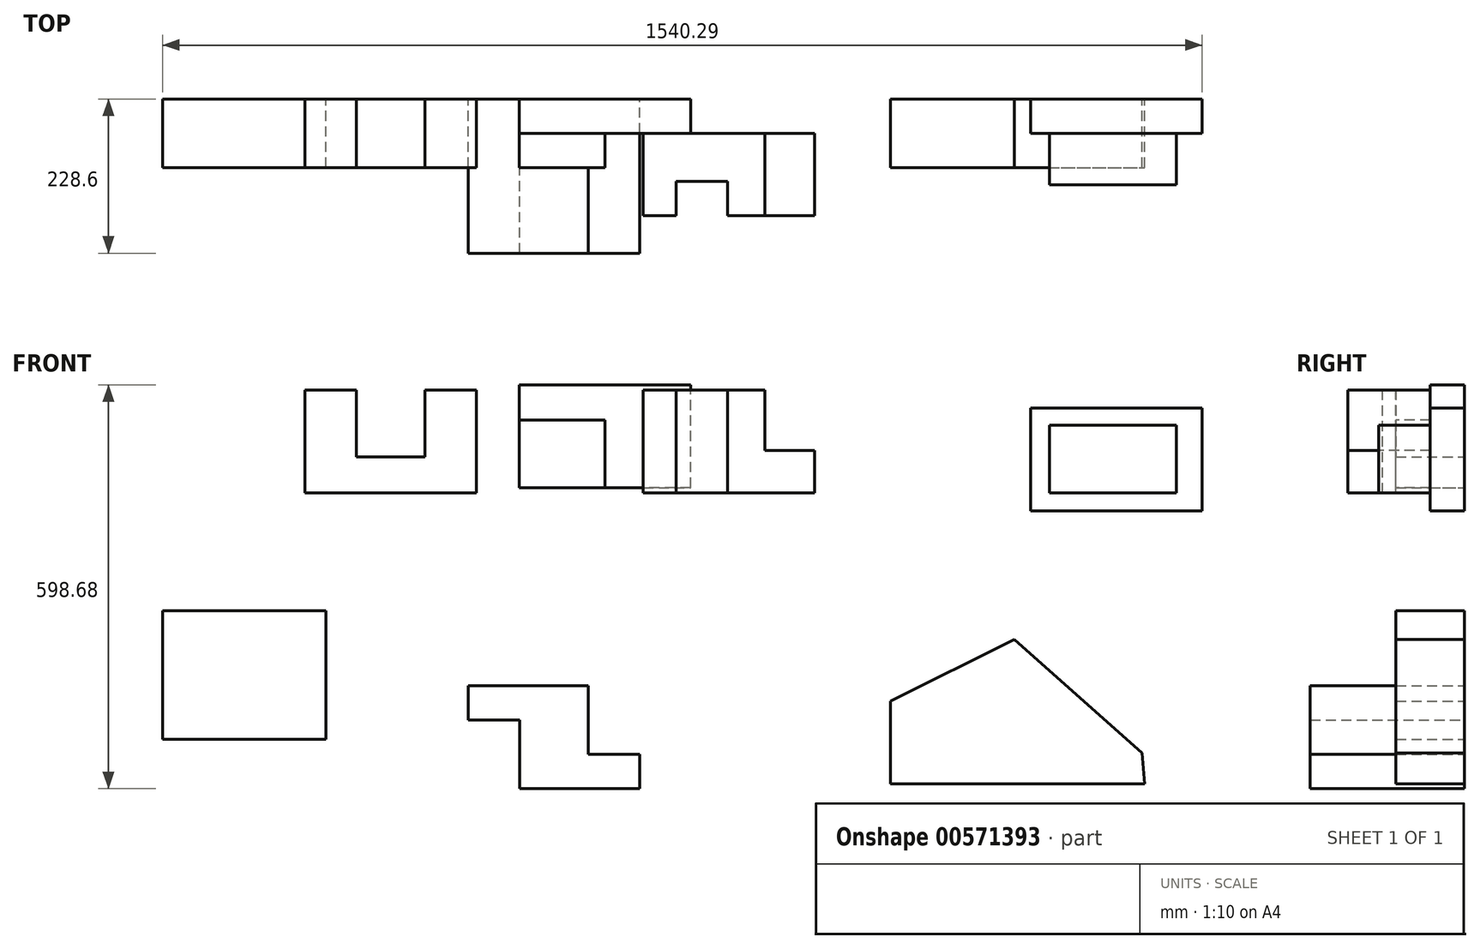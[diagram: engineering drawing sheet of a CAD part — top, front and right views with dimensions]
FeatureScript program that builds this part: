
annotation { "Feature Type Name" : "Feature", "Feature Type Description" : "" }
export const myFeature = defineFeature(function(context is Context, id is Id, definition is map)
    precondition{}
    {
        {
            var Q0;
            Q0=qCreatedBy(makeId("Front.planeOp"),FACE);
            var sketch = newSketch(context, id + "F0", { "sketchPlane" : qUnion([Q0])});
            skLineSegment(sketch, "E0", {"start": v(254, 0) * mm, "end": v(254, 152.4) * mm});
            skLineSegment(sketch, "E1", {"start": v(254, 152.4) * mm, "end": v(177.8, 152.4) * mm});
            skLineSegment(sketch, "E2", {"start": v(177.8, 152.4) * mm, "end": v(177.8, 53.07) * mm});
            skLineSegment(sketch, "E3", {"start": v(177.8, 53.07) * mm, "end": v(76.2, 53.07) * mm});
            skLineSegment(sketch, "E4", {"start": v(76.2, 53.07) * mm, "end": v(76.2, 152.4) * mm});
            skLineSegment(sketch, "E5", {"start": v(76.2, 152.4) * mm, "end": v(0, 152.4) * mm});
            skLineSegment(sketch, "E6", {"start": v(0, 152.4) * mm, "end": v(0, 0) * mm});
            skLineSegment(sketch, "E7", {"start": v(0, 0) * mm, "end": v(254, 0) * mm});
            skSolve(sketch);
        }
        {
            var Q0;
            Q0=makeQuery(id+"F0.imprint","IMPRINT",FACE,{"disambiguationData":[TD([[makeQuery(id+"F0.imprint","IMPRINT",EDGE,{"derivedFrom":sQuery(id+"F0.wireOp",EDGE,"E0")}),1.0]])]});
            extrude(context, id + "F1", {"entities" : qUnion([Q0]), "depth" : 101.6 * mm, "offsetDistance" : 25.4 * mm});
        }
        {
            var Q0;
            Q0=qCreatedBy(makeId("Front.planeOp"),FACE);
            var sketch = newSketch(context, id + "F2", { "sketchPlane" : qUnion([Q0])});
            skLineSegment(sketch, "E8.bottom", {"start": v(317.16, 7.63) * mm, "end": v(571.16, 7.63) * mm});
            skLineSegment(sketch, "E8.top", {"start": v(317.16, 160.03) * mm, "end": v(571.16, 160.03) * mm});
            skLineSegment(sketch, "E8.left", {"start": v(317.16, 7.63) * mm, "end": v(317.16, 160.03) * mm});
            skLineSegment(sketch, "E8.right", {"start": v(571.16, 7.63) * mm, "end": v(571.16, 160.03) * mm});
            skSolve(sketch);
        }
        {
            var Q0;
            Q0=makeQuery(id+"F2.imprint","IMPRINT",FACE,{"disambiguationData":[TD([[makeQuery(id+"F2.imprint","IMPRINT",EDGE,{"derivedFrom":sQuery(id+"F2.wireOp",EDGE,"E8.bottom")}),1.0]])]});
            extrude(context, id + "F3", {"entities" : qUnion([Q0]), "depth" : 101.6 * mm, "offsetDistance" : 25.4 * mm});
        }
        {
            var Q0;
            Q0=makeQuery(id+"F3.opExtrude","SWEPT_FACE",FACE,{"disambiguationData":[OSD([sQuery(id+"F2.wireOp",EDGE,"E8.top")])]});
            var sketch = newSketch(context, id + "F4", { "sketchPlane" : qUnion([Q0])});
            skLineSegment(sketch, "E9.bottom", {"start": v(571.16, -50.8) * mm, "end": v(444.16, -50.8) * mm});
            skLineSegment(sketch, "E9.top", {"start": v(571.16, -101.6) * mm, "end": v(444.16, -101.6) * mm});
            skLineSegment(sketch, "E9.left", {"start": v(571.16, -50.8) * mm, "end": v(571.16, -101.6) * mm});
            skLineSegment(sketch, "E9.right", {"start": v(444.16, -50.8) * mm, "end": v(444.16, -101.6) * mm});
            skSolve(sketch);
        }
        {
            var Q0;
            Q0=makeQuery(id+"F4.imprint","IMPRINT",FACE,{"disambiguationData":[TD([[makeQuery(id+"F4.imprint","IMPRINT",EDGE,{"derivedFrom":sQuery(id+"F4.wireOp",EDGE,"E9.bottom")}),1.0]])]});
            extrude(context, id + "F5", {"entities" : qUnion([Q0]), "operationType" : NewBodyOperationType.REMOVE, "oppositeDirection" : true, "depth" : 152.4 * mm, "offsetDistance" : 25.4 * mm});
        }
        {
            var Q0;
            Q0=makeQuery(id+"F3.opExtrude","CAP_FACE",FACE,{"disambiguationData":[OSD([sQuery(id+"F2.wireOp",EDGE,"E8.bottom"),sQuery(id+"F2.wireOp",EDGE,"E8.top"),sQuery(id+"F2.wireOp",EDGE,"E8.left"),sQuery(id+"F2.wireOp",EDGE,"E8.right")])],"isStart":false});
            var sketch = newSketch(context, id + "F6", { "sketchPlane" : qUnion([Q0])});
            skLineSegment(sketch, "E10.bottom", {"start": v(317.16, 160.03) * mm, "end": v(444.16, 160.03) * mm});
            skLineSegment(sketch, "E10.top", {"start": v(317.16, 107.58) * mm, "end": v(444.16, 107.58) * mm});
            skLineSegment(sketch, "E10.left", {"start": v(317.16, 160.03) * mm, "end": v(317.16, 107.58) * mm});
            skLineSegment(sketch, "E10.right", {"start": v(444.16, 160.03) * mm, "end": v(444.16, 107.58) * mm});
            skSolve(sketch);
        }
        {
            var Q0;
            Q0=makeQuery(id+"F6.imprint","IMPRINT",FACE,{"disambiguationData":[TD([[makeQuery(id+"F6.imprint","IMPRINT",EDGE,{"derivedFrom":sQuery(id+"F6.wireOp",EDGE,"E10.bottom")}),-1.0]])]});
            extrude(context, id + "F7", {"entities" : qUnion([Q0]), "operationType" : NewBodyOperationType.REMOVE, "oppositeDirection" : true, "depth" : 50.8 * mm, "offsetDistance" : 25.4 * mm});
        }
        {
            var Q0;
            Q0=makeQuery(id+"F7.boolean.opBoolean","MERGE",FACE,{"derivedFrom":[makeQuery(id+"F5.boolean.opBoolean","COPY",FACE,{"derivedFrom":makeQuery(id+"F5.opExtrude","SWEPT_FACE",FACE,{"disambiguationData":[OSD([sQuery(id+"F4.wireOp",EDGE,"E9.bottom")])]})}),makeQuery(id+"F7.opExtrude","CAP_FACE",FACE,{"disambiguationData":[OSD([sQuery(id+"F6.wireOp",EDGE,"E10.bottom"),sQuery(id+"F6.wireOp",EDGE,"E10.top"),sQuery(id+"F6.wireOp",EDGE,"E10.left"),sQuery(id+"F6.wireOp",EDGE,"E10.right")])],"isStart":false})]});
            var sketch = newSketch(context, id + "F8", { "sketchPlane" : qUnion([Q0])});
            skLineSegment(sketch, "E11.bottom", {"start": v(500.85, 152.4) * mm, "end": v(754.85, 152.4) * mm});
            skLineSegment(sketch, "E11.top", {"start": v(500.85, 0) * mm, "end": v(754.85, 0) * mm});
            skLineSegment(sketch, "E11.left", {"start": v(500.85, 152.4) * mm, "end": v(500.85, 0) * mm});
            skLineSegment(sketch, "E11.right", {"start": v(754.85, 152.4) * mm, "end": v(754.85, 0) * mm});
            skSolve(sketch);
        }
        {
            var Q0;
            Q0 = qSketchRegion(id + "F8", true);
            extrude(context, id + "F9", {"entities" : qUnion([Q0]), "operationType" : NewBodyOperationType.ADD, "depth" : 121.92 * mm, "offsetDistance" : 25.4 * mm});
        }
        {
            var Q0;
            Q0=makeQuery(id+"F9.opExtrude","CAP_FACE",FACE,{"disambiguationData":[OSD([sQuery(id+"F8.wireOp",EDGE,"E11.bottom"),sQuery(id+"F8.wireOp",EDGE,"E11.top"),sQuery(id+"F8.wireOp",EDGE,"E11.left"),sQuery(id+"F8.wireOp",EDGE,"E11.right")])],"isStart":false});
            var sketch = newSketch(context, id + "F10", { "sketchPlane" : qUnion([Q0])});
            skLineSegment(sketch, "E12.bottom", {"start": v(551.65, 152.4) * mm, "end": v(500.85, 152.4) * mm});
            skLineSegment(sketch, "E12.top", {"start": v(551.65, 0) * mm, "end": v(500.85, 0) * mm});
            skLineSegment(sketch, "E12.left", {"start": v(551.65, 152.4) * mm, "end": v(551.65, 0) * mm});
            skLineSegment(sketch, "E12.right", {"start": v(500.85, 152.4) * mm, "end": v(500.85, 0) * mm});
            skSolve(sketch);
        }
        {
            var Q0;
            {var subQ0=sQuery(id+"F10.wireOp",EDGE,"E12.left");Q0=makeQuery(id+"F10.imprint","IMPRINT",FACE,{"disambiguationData":[TD([[makeQuery(id+"F10.imprint","IMPRINT",EDGE,{"derivedFrom":subQ0}),1.0]])]});}
            var sketch = newSketch(context, id + "F11", { "sketchPlane" : qUnion([Q0])});
            skLineSegment(sketch, "E13.bottom", {"start": v(757.59, 164.43) * mm, "end": v(681.39, 164.43) * mm});
            skLineSegment(sketch, "E13.top", {"start": v(757.59, 62.83) * mm, "end": v(681.39, 62.83) * mm});
            skLineSegment(sketch, "E13.left", {"start": v(757.59, 164.43) * mm, "end": v(757.59, 62.83) * mm});
            skLineSegment(sketch, "E13.right", {"start": v(681.39, 164.43) * mm, "end": v(681.39, 62.83) * mm});
            skSolve(sketch);
        }
        {
            var Q0;
            Q0 = qSketchRegion(id + "F11", true);
            extrude(context, id + "F12", {"entities" : qUnion([Q0]), "operationType" : NewBodyOperationType.REMOVE, "oppositeDirection" : true, "depth" : 152.4 * mm, "offsetDistance" : 25.4 * mm});
        }
        {
            var Q0;
            {var subQ0=sQuery(id+"F10.wireOp",EDGE,"E12.left");Q0=makeQuery(id+"F10.imprint","IMPRINT",FACE,{"disambiguationData":[TD([[makeQuery(id+"F10.imprint","IMPRINT",EDGE,{"derivedFrom":subQ0}),1.0]])]});}
            var sketch = newSketch(context, id + "F13", { "sketchPlane" : qUnion([Q0])});
            skSolve(sketch);
        }
        {
            var Q0;
            Q0=qCreatedBy(makeId("Front.planeOp"),FACE);
            var sketch = newSketch(context, id + "F14", { "sketchPlane" : qUnion([Q0])});
            skLineSegment(sketch, "E14.bottom", {"start": v(-211.06, -175.13) * mm, "end": v(31.18, -175.13) * mm});
            skLineSegment(sketch, "E14.top", {"start": v(-211.06, -365.46) * mm, "end": v(31.18, -365.46) * mm});
            skLineSegment(sketch, "E14.left", {"start": v(-211.06, -175.13) * mm, "end": v(-211.06, -365.46) * mm});
            skLineSegment(sketch, "E14.right", {"start": v(31.18, -175.13) * mm, "end": v(31.18, -365.46) * mm});
            skSolve(sketch);
        }
        {
            var Q0;
            Q0 = qSketchRegion(id + "F14", true);
            extrude(context, id + "F15", {"entities" : qUnion([Q0]), "depth" : 101.6 * mm, "offsetDistance" : 25.4 * mm});
        }
        {
            var Q0;
            Q0=qCreatedBy(makeId("Front.planeOp"),FACE);
            var sketch = newSketch(context, id + "F16", { "sketchPlane" : qUnion([Q0])});
            skLineSegment(sketch, "E15", {"start": v(242.02, -286.25) * mm, "end": v(419.82, -286.25) * mm});
            skLineSegment(sketch, "E16", {"start": v(419.82, -286.25) * mm, "end": v(419.82, -387.85) * mm});
            skLineSegment(sketch, "E17", {"start": v(419.82, -387.85) * mm, "end": v(496.02, -387.85) * mm});
            skLineSegment(sketch, "E18", {"start": v(496.02, -387.85) * mm, "end": v(496.02, -438.65) * mm});
            skLineSegment(sketch, "E19", {"start": v(242.02, -286.25) * mm, "end": v(242.02, -337.05) * mm});
            skLineSegment(sketch, "E20", {"start": v(242.02, -337.05) * mm, "end": v(318.22, -337.05) * mm});
            skLineSegment(sketch, "E21", {"start": v(318.22, -337.05) * mm, "end": v(318.22, -438.65) * mm});
            skLineSegment(sketch, "E22", {"start": v(318.22, -438.65) * mm, "end": v(496.02, -438.65) * mm});
            skSolve(sketch);
        }
        {
            var Q0;
            Q0=makeQuery(id+"F16.imprint","IMPRINT",FACE,{"disambiguationData":[TD([[makeQuery(id+"F16.imprint","IMPRINT",EDGE,{"derivedFrom":sQuery(id+"F16.wireOp",EDGE,"E15")}),-1.0]])]});
            extrude(context, id + "F17", {"entities" : qUnion([Q0]), "depth" : 101.6 * mm, "offsetDistance" : 25.4 * mm});
        }
        {
            var Q0;
            Q0=makeQuery(id+"F17.opExtrude","CAP_FACE",FACE,{"disambiguationData":[OSD([sQuery(id+"F16.wireOp",EDGE,"E15"),sQuery(id+"F16.wireOp",EDGE,"E16"),sQuery(id+"F16.wireOp",EDGE,"E17"),sQuery(id+"F16.wireOp",EDGE,"E18"),sQuery(id+"F16.wireOp",EDGE,"E19"),sQuery(id+"F16.wireOp",EDGE,"E20"),sQuery(id+"F16.wireOp",EDGE,"E21"),sQuery(id+"F16.wireOp",EDGE,"E22")])],"isStart":false});
            var sketch = newSketch(context, id + "F18", { "sketchPlane" : qUnion([Q0])});
            skSolve(sketch);
        }
        {
            var Q0;
            Q0=makeQuery(id+"F18.imprint","IMPRINT",FACE,{"disambiguationData":[TD([[makeQuery(id+"F18.imprint","IMPRINT",EDGE,{"derivedFrom":makeQuery(id+"F17.opExtrude","CAP_EDGE",EDGE,{"disambiguationData":[OSD([sQuery(id+"F16.wireOp",EDGE,"E15")])],"isStart":false})}),-1.0]])]});
            var sketch = newSketch(context, id + "F19", { "sketchPlane" : qUnion([Q0])});
            skSolve(sketch);
        }
        {
            var Q0;
            Q0=makeQuery(id+"F19.imprint","IMPRINT",FACE,{"disambiguationData":[TD([[makeQuery(id+"F19.imprint","IMPRINT",EDGE,{"derivedFrom":makeQuery(id+"F18.imprint","IMPRINT",EDGE,{"derivedFrom":makeQuery(id+"F17.opExtrude","CAP_EDGE",EDGE,{"disambiguationData":[OSD([sQuery(id+"F16.wireOp",EDGE,"E15")])],"isStart":false})})}),-1.0]])]});
            var Q1;
            Q1=makeQuery(id+"F18.imprint","IMPRINT",FACE,{"disambiguationData":[TD([[makeQuery(id+"F18.imprint","IMPRINT",EDGE,{"derivedFrom":makeQuery(id+"F17.opExtrude","CAP_EDGE",EDGE,{"disambiguationData":[OSD([sQuery(id+"F16.wireOp",EDGE,"E15")])],"isStart":false})}),-1.0]])]});
            var Q2;
            Q2=makeQuery(id+"F17.opExtrude","CAP_FACE",FACE,{"disambiguationData":[OSD([sQuery(id+"F16.wireOp",EDGE,"E15"),sQuery(id+"F16.wireOp",EDGE,"E16"),sQuery(id+"F16.wireOp",EDGE,"E17"),sQuery(id+"F16.wireOp",EDGE,"E18"),sQuery(id+"F16.wireOp",EDGE,"E19"),sQuery(id+"F16.wireOp",EDGE,"E20"),sQuery(id+"F16.wireOp",EDGE,"E21"),sQuery(id+"F16.wireOp",EDGE,"E22")])],"isStart":false});
            var Q3;
            Q3=makeQuery(id+"F17.opExtrude","CAP_FACE",FACE,{"disambiguationData":[OSD([sQuery(id+"F16.wireOp",EDGE,"E15"),sQuery(id+"F16.wireOp",EDGE,"E16"),sQuery(id+"F16.wireOp",EDGE,"E17"),sQuery(id+"F16.wireOp",EDGE,"E18"),sQuery(id+"F16.wireOp",EDGE,"E19"),sQuery(id+"F16.wireOp",EDGE,"E20"),sQuery(id+"F16.wireOp",EDGE,"E21"),sQuery(id+"F16.wireOp",EDGE,"E22")])],"isStart":true});
            extrude(context, id + "F20", {"entities" : qUnion([Q0, Q1, Q2, Q3]), "operationType" : NewBodyOperationType.ADD, "depth" : 127 * mm, "offsetDistance" : 25.4 * mm});
        }
        {
            var Q0;
            Q0=qCreatedBy(makeId("Front.planeOp"),FACE);
            var sketch = newSketch(context, id + "F21", { "sketchPlane" : qUnion([Q0])});
            skLineSegment(sketch, "E23", {"start": v(867.45, -431.57) * mm, "end": v(1244.14, -431.57) * mm});
            skLineSegment(sketch, "E24", {"start": v(867.45, -431.57) * mm, "end": v(867.45, -308.9) * mm});
            skLineSegment(sketch, "E25", {"start": v(867.45, -308.9) * mm, "end": v(1050.84, -217.2) * mm});
            skLineSegment(sketch, "E26", {"start": v(1050.84, -217.2) * mm, "end": v(1240.43, -385.72) * mm});
            skLineSegment(sketch, "E27", {"start": v(1240.43, -385.72) * mm, "end": v(1244.14, -431.57) * mm});
            skSolve(sketch);
        }
        {
            var Q0;
            Q0=qCreatedBy(makeId("Front.planeOp"),FACE);
            var sketch = newSketch(context, id + "F22", { "sketchPlane" : qUnion([Q0])});
            skLineSegment(sketch, "E28.bottom", {"start": v(1075.23, 125.37) * mm, "end": v(1329.23, 125.37) * mm});
            skLineSegment(sketch, "E28.top", {"start": v(1075.23, -27.03) * mm, "end": v(1329.23, -27.03) * mm});
            skLineSegment(sketch, "E28.left", {"start": v(1075.23, 125.37) * mm, "end": v(1075.23, -27.03) * mm});
            skLineSegment(sketch, "E28.right", {"start": v(1329.23, 125.37) * mm, "end": v(1329.23, -27.03) * mm});
            skSolve(sketch);
        }
        {
            var Q0;
            Q0=makeQuery(id+"F22.imprint","IMPRINT",FACE,{"disambiguationData":[TD([[makeQuery(id+"F22.imprint","IMPRINT",EDGE,{"derivedFrom":sQuery(id+"F22.wireOp",EDGE,"E28.bottom")}),-1.0]])]});
            extrude(context, id + "F23", {"entities" : qUnion([Q0]), "depth" : 50.8 * mm, "offsetDistance" : 25.4 * mm});
        }
        {
            var Q0;
            Q0=makeQuery(id+"F21.imprint","IMPRINT",FACE,{"disambiguationData":[TD([[makeQuery(id+"F21.imprint","IMPRINT",EDGE,{"derivedFrom":sQuery(id+"F21.wireOp",EDGE,"E23")}),1.0]])]});
            extrude(context, id + "F24", {"entities" : qUnion([Q0]), "depth" : 101.6 * mm, "offsetDistance" : 25.4 * mm});
        }
        {
            var Q0;
            Q0=makeQuery(id+"F24.opExtrude","CAP_FACE",FACE,{"disambiguationData":[OSD([sQuery(id+"F21.wireOp",EDGE,"E23"),sQuery(id+"F21.wireOp",EDGE,"E24"),sQuery(id+"F21.wireOp",EDGE,"E25"),sQuery(id+"F21.wireOp",EDGE,"E26"),sQuery(id+"F21.wireOp",EDGE,"E27")])],"isStart":false});
            var sketch = newSketch(context, id + "F25", { "sketchPlane" : qUnion([Q0])});
            skSolve(sketch);
        }
        {
            var Q0;
            Q0=makeQuery(id+"F23.opExtrude","CAP_FACE",FACE,{"disambiguationData":[OSD([sQuery(id+"F22.wireOp",EDGE,"E28.bottom"),sQuery(id+"F22.wireOp",EDGE,"E28.top"),sQuery(id+"F22.wireOp",EDGE,"E28.left"),sQuery(id+"F22.wireOp",EDGE,"E28.right")])],"isStart":false});
            var sketch = newSketch(context, id + "F26", { "sketchPlane" : qUnion([Q0])});
            skSolve(sketch);
        }
        {
            var Q0;
            Q0=makeQuery(id+"F26.imprint","IMPRINT",FACE,{"disambiguationData":[TD([[makeQuery(id+"F26.imprint","IMPRINT",EDGE,{"derivedFrom":makeQuery(id+"F23.opExtrude","CAP_EDGE",EDGE,{"disambiguationData":[OSD([sQuery(id+"F22.wireOp",EDGE,"E28.bottom")])],"isStart":false})}),-1.0]])]});
            var sketch = newSketch(context, id + "F27", { "sketchPlane" : qUnion([Q0])});
            skLineSegment(sketch, "E29.bottom", {"start": v(1102.85, 99.9) * mm, "end": v(1290.78, 99.9) * mm});
            skLineSegment(sketch, "E29.top", {"start": v(1102.85, 0) * mm, "end": v(1290.78, 0) * mm});
            skLineSegment(sketch, "E29.left", {"start": v(1102.85, 99.9) * mm, "end": v(1102.85, 0) * mm});
            skLineSegment(sketch, "E29.right", {"start": v(1290.78, 99.9) * mm, "end": v(1290.78, 0) * mm});
            skSolve(sketch);
        }
        {
            var Q0;
            Q0 = qSketchRegion(id + "F27", true);
            extrude(context, id + "F28", {"entities" : qUnion([Q0]), "operationType" : NewBodyOperationType.ADD, "depth" : 76.2 * mm, "offsetDistance" : 25.4 * mm});
        }
        {
            var Q0;
            {var subQ0=sQuery(id+"F10.wireOp",EDGE,"E12.left");Q0=makeQuery(id+"F13.imprint","IMPRINT",FACE,{"disambiguationData":[TD([[makeQuery(id+"F13.imprint","IMPRINT",EDGE,{"derivedFrom":makeQuery(id+"F10.imprint","IMPRINT",EDGE,{"derivedFrom":subQ0})}),1.0]])]});}
            var sketch = newSketch(context, id + "F29", { "sketchPlane" : qUnion([Q0])});
            skLineSegment(sketch, "E30.bottom", {"start": v(550.05, 153.44) * mm, "end": v(626.25, 153.44) * mm});
            skLineSegment(sketch, "E30.top", {"start": v(550.05, 0) * mm, "end": v(626.25, 0) * mm});
            skLineSegment(sketch, "E30.left", {"start": v(550.05, 153.44) * mm, "end": v(550.05, 0) * mm});
            skLineSegment(sketch, "E30.right", {"start": v(626.25, 153.44) * mm, "end": v(626.25, 0) * mm});
            skSolve(sketch);
        }
        {
            var Q0;
            Q0 = qSketchRegion(id + "F29", true);
            extrude(context, id + "F30", {"entities" : qUnion([Q0]), "operationType" : NewBodyOperationType.REMOVE, "oppositeDirection" : true, "depth" : 50.8 * mm, "offsetDistance" : 25.4 * mm});
        }
    });
